# Revit family: BC_Hitachi_RPI-FSNE-8-10.0_LOD400
name_source: partatom
category: Equipement de génie climatique
revit_build: Autodesk Revit 2016 (Build: 20150220_1215(x64)
units: mm (PartAtom-declared; Revit-internal decimal feet)

## family parameters
Basée sur le plan de construction = Non
Cote de connecteur circulaire = Utiliser le diamètre
Couper avec des vides une fois chargée = Non
Numéro OmniClass = 23.75.00.00
Partagée = Non
Point de calcul de pièce = Non
Titre OmniClass = Climate Control (HVAC)
Toujours verticalement = Oui
Type d'élément = Normal

## types (2) — shared parameters
Air flow Speed (high/medium/low) m3/min) = 66/66/60
Air outlet distance = 25.00 mm
Description = Duct High pressure, Up to 200 Pa
Distance from left Drain pipe = 370.00 mm
Drain pipe Height = 20.00 mm
Fabricant = HITACHI
Fan motor type (output) = 1065 W
Frequency = 50 Hz
Gas pipe Height = 250.00 mm
Input Height = 324.00 mm
Input Width = 1376.00 mm
Liquid Diameter = 9.52 mm
Liquid pipe Height = 300.00 mm
Maximum AC Voltage = 253 V
Maximum Air Flow = 66000.0 L/min
Maximum running current = 10 A
Minimum AC Voltage = 207 V
Minimum Air Flow = 60000.0 L/min
Modèle = Ducted unit RPI-FSN3/4 - 8 to 10
Number of Poles = 1
Operation and Service pipe distance = 600.00 mm
Outlet Diameter = 25.00 mm
Output Height = 250.00 mm
Output Width = 866.00 mm
Overall Depth = 423.00 mm
Overall Height = 1594.00 mm
Overall Width = 600.00 mm
Power supply = 230 V
Refrigerant = R410A

## per-type parameters (varying)
| type | Cooling Capacity | Distance from left liquid pipe | Distance from left pipe | Gas Diameter | Heating Capacity | Mass | Product Code | Sound power at medium load (dB(A)) | Sound power at minimal load (dB(A)) | Sound power level dB(A) | Sound power max (dB(A)) |
| RPI - 8.0 FSN3E | 22 kW | 360.00 mm | 360.00 mm | 20.00 mm | 25 kW | 85.00 kg | 7E424410 | 54 | 51 | 77 | 54 |
| RPI - 10.0 FSN3E | 28 kW | 370.00 mm | 370.00 mm | 22.20 mm | 31 kW | 87.00 kg | 7E424411 | 55 | 52 | 78 | 55 |

note: column(s) folded — value = type name in every type: Commentaires du type

## geometry (parser evidence)
native form markers: Blend x2
no freeform markers — native parametric forms only
